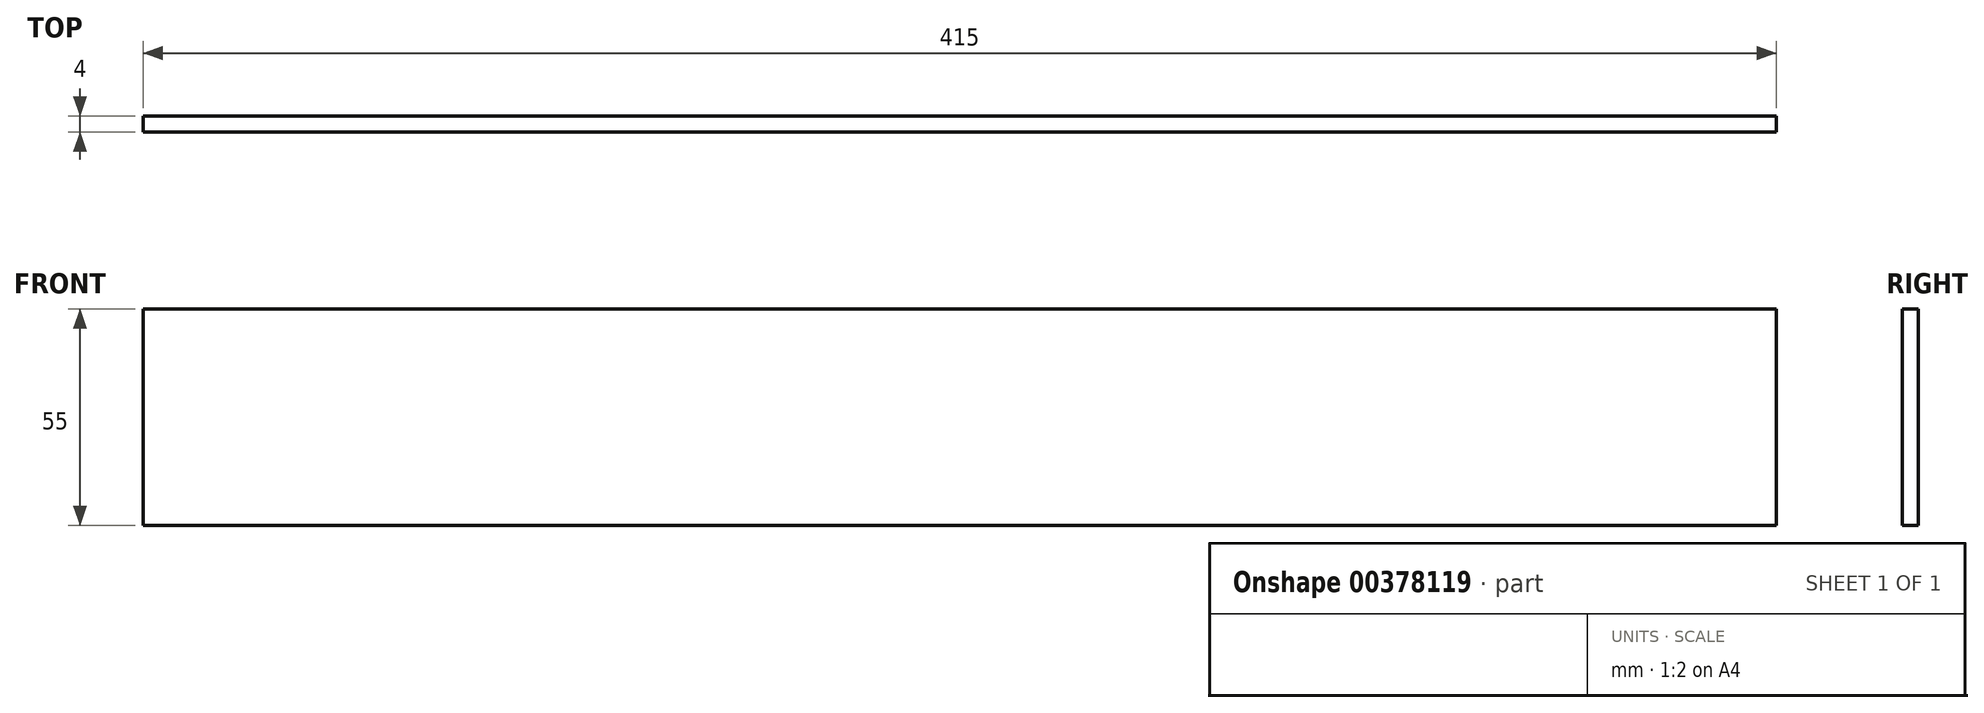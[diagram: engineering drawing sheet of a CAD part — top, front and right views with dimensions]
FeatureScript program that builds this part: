
annotation { "Feature Type Name" : "Feature", "Feature Type Description" : "" }
export const myFeature = defineFeature(function(context is Context, id is Id, definition is map)
    precondition{}
    {
        {
            var Q0;
            Q0=qCreatedBy(makeId("Front.planeOp"),FACE);
            var sketch = newSketch(context, id + "F0", { "sketchPlane" : qUnion([Q0])});
            skLineSegment(sketch, "E0.bottom", {"start": v(0, 0) * mm, "end": v(415, 0) * mm});
            skLineSegment(sketch, "E0.top", {"start": v(0, 55) * mm, "end": v(415, 55) * mm});
            skLineSegment(sketch, "E0.left", {"start": v(0, 0) * mm, "end": v(0, 55) * mm});
            skLineSegment(sketch, "E0.right", {"start": v(415, 0) * mm, "end": v(415, 55) * mm});
            skSolve(sketch);
        }
        {
            var Q0;
            Q0=makeQuery(id+"F0.imprint","IMPRINT",FACE,{"disambiguationData":[TD([[makeQuery(id+"F0.imprint","IMPRINT",EDGE,{"derivedFrom":sQuery(id+"F0.wireOp",EDGE,"E0.bottom")}),1.0]])]});
            extrude(context, id + "F1", {"entities" : qUnion([Q0]), "depth" : 4 * mm});
        }
    });
